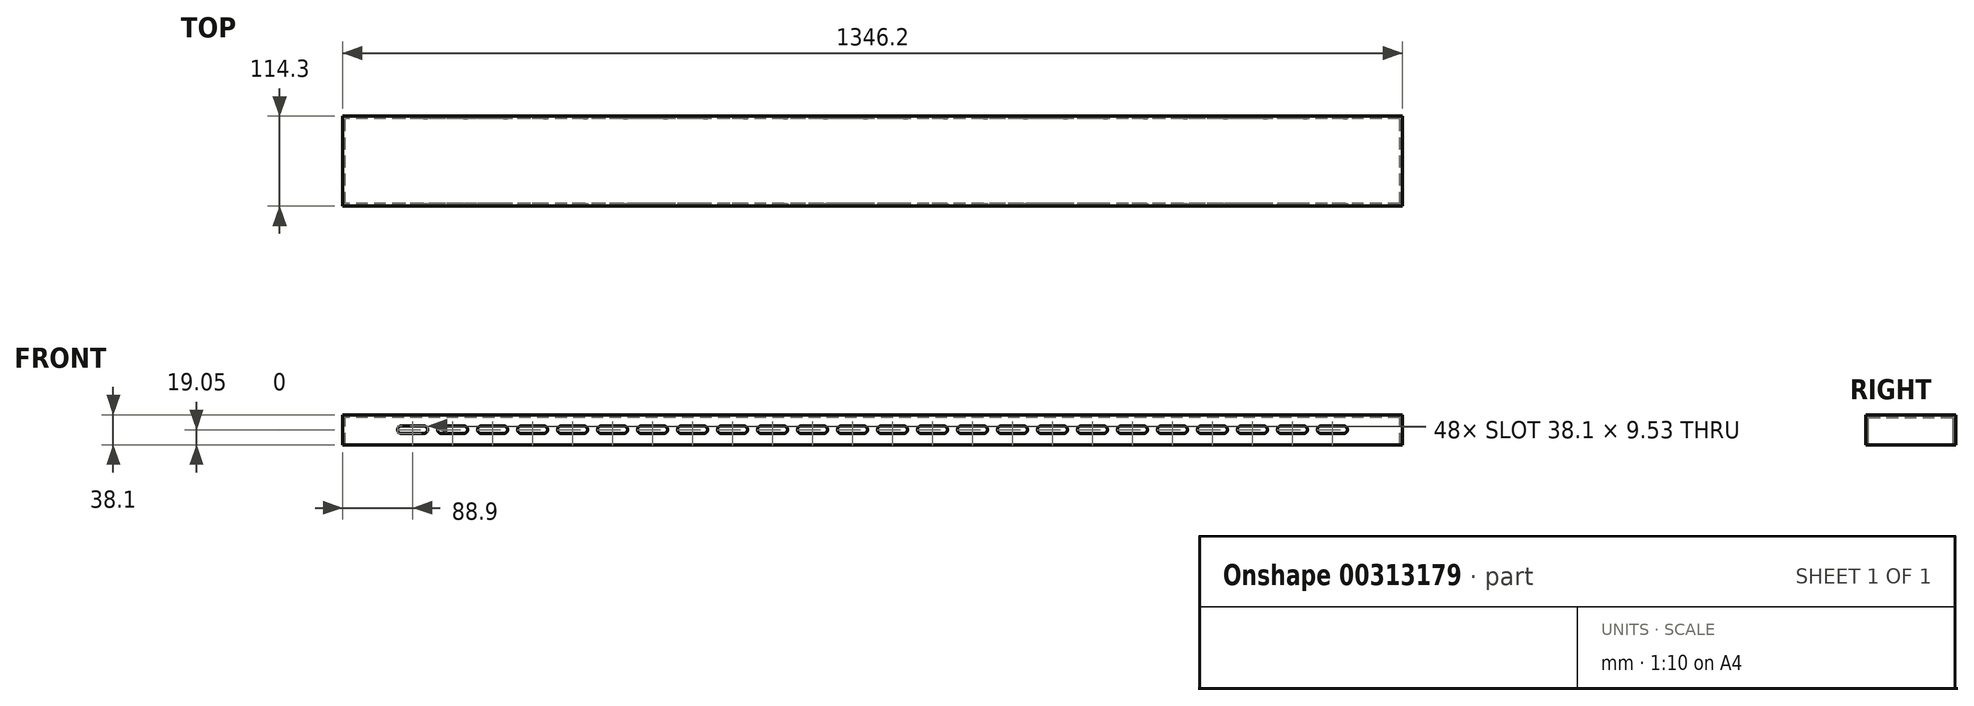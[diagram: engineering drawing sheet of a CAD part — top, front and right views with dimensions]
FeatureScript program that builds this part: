
annotation { "Feature Type Name" : "Feature", "Feature Type Description" : "" }
export const myFeature = defineFeature(function(context is Context, id is Id, definition is map)
    precondition{}
    {
        {
            var Q0;
            Q0=qCreatedBy(makeId("Right.planeOp"),FACE);
            var sketch = newSketch(context, id + "F0", { "sketchPlane" : qUnion([Q0])});
            skLineSegment(sketch, "E0.bottom", {"start": v(0, 0) * mm, "end": v(114.3, 0) * mm});
            skLineSegment(sketch, "E0.top", {"start": v(0, 38.1) * mm, "end": v(114.3, 38.1) * mm});
            skLineSegment(sketch, "E0.left", {"start": v(0, 0) * mm, "end": v(0, 38.1) * mm});
            skLineSegment(sketch, "E0.right", {"start": v(114.3, 0) * mm, "end": v(114.3, 38.1) * mm});
            skSolve(sketch);
        }
        {
            var Q0;
            Q0=qSketchRegion(id+"F0",true);
            extrude(context, id + "F1", {"entities" : qUnion([Q0]), "endBound" : BoundingType.SYMMETRIC, "depth" : 1346.2 * mm});
        }
        {
            var Q0;
            Q0=makeQuery(id+"F1.opExtrude","SWEPT_FACE",FACE,{"disambiguationData":[OSD([sQuery(id+"F0.wireOp",EDGE,"E0.bottom")])]});
            shell(context, id + "F2", {"entities" : qUnion([Q0]), "thickness" : 3.17 * mm});
        }
        {
            var Q0;
            Q0=makeQuery(id+"F1.opExtrude","SWEPT_FACE",FACE,{"disambiguationData":[OSD([sQuery(id+"F0.wireOp",EDGE,"E0.left")])]});
            var sketch = newSketch(context, id + "F3", { "sketchPlane" : qUnion([Q0])});
            skPoint(sketch, "E1.centerSnap0", {"position": v(-673.1, 19.05) * mm});
            skLineSegment(sketch, "E2.bottom", {"start": v(-569.91, 14.29) * mm, "end": v(-598.49, 14.29) * mm});
            skLineSegment(sketch, "E2.top", {"start": v(-569.91, 23.81) * mm, "end": v(-598.49, 23.81) * mm});
            skLineSegment(sketch, "E2.left", {"start": v(-565.15, 19.05) * mm, "end": v(-565.15, 19.05) * mm});
            skLineSegment(sketch, "E2.right", {"start": v(-603.25, 19.05) * mm, "end": v(-603.25, 19.05) * mm});
            skPoint(sketch, "E2.middle", {"position": v(-584.2, 19.05) * mm});
            skPoint(sketch, "E3.visualSharp", {"position": v(-565.15, 23.81) * mm});
            skArc(sketch, "E3.filletArc", {"start": v(-565.15, 19.05) * mm, "mid": v(-566.54, 22.42) * mm, "end": v(-569.91, 23.81) * mm});
            skPoint(sketch, "E4.visualSharp", {"position": v(-565.15, 14.29) * mm});
            skArc(sketch, "E4.filletArc", {"start": v(-569.91, 14.29) * mm, "mid": v(-566.54, 15.68) * mm, "end": v(-565.15, 19.05) * mm});
            skPoint(sketch, "E5.visualSharp", {"position": v(-603.25, 23.81) * mm});
            skArc(sketch, "E5.filletArc", {"start": v(-598.49, 23.81) * mm, "mid": v(-601.86, 22.42) * mm, "end": v(-603.25, 19.05) * mm});
            skPoint(sketch, "E6.visualSharp", {"position": v(-603.25, 14.29) * mm});
            skArc(sketch, "E6.filletArc", {"start": v(-603.25, 19.05) * mm, "mid": v(-601.86, 15.68) * mm, "end": v(-598.49, 14.29) * mm});
            skPoint(sketch, "E7.1.0.0", {"position": v(-514.35, 14.29) * mm});
            skPoint(sketch, "E7.1.0.1", {"position": v(-514.35, 23.81) * mm});
            skLineSegment(sketch, "E7.1.0.2", {"start": v(-519.11, 23.81) * mm, "end": v(-547.69, 23.81) * mm});
            skPoint(sketch, "E7.1.0.3", {"position": v(-552.45, 14.29) * mm});
            skLineSegment(sketch, "E7.1.0.4", {"start": v(-519.11, 14.29) * mm, "end": v(-547.69, 14.29) * mm});
            skPoint(sketch, "E7.1.0.5", {"position": v(-533.4, 19.05) * mm});
            skPoint(sketch, "E7.1.0.6", {"position": v(-552.45, 23.81) * mm});
            skArc(sketch, "E7.1.0.7", {"start": v(-514.35, 19.05) * mm, "mid": v(-515.74, 22.42) * mm, "end": v(-519.11, 23.81) * mm});
            skArc(sketch, "E7.1.0.8", {"start": v(-519.11, 14.29) * mm, "mid": v(-515.74, 15.68) * mm, "end": v(-514.35, 19.05) * mm});
            skArc(sketch, "E7.1.0.9", {"start": v(-552.45, 19.05) * mm, "mid": v(-551.06, 15.68) * mm, "end": v(-547.69, 14.29) * mm});
            skArc(sketch, "E7.1.0.10", {"start": v(-547.69, 23.81) * mm, "mid": v(-551.06, 22.42) * mm, "end": v(-552.45, 19.05) * mm});
            skPoint(sketch, "E7.2.0.0", {"position": v(-463.55, 14.29) * mm});
            skPoint(sketch, "E7.2.0.1", {"position": v(-463.55, 23.81) * mm});
            skLineSegment(sketch, "E7.2.0.2", {"start": v(-468.31, 23.81) * mm, "end": v(-496.89, 23.81) * mm});
            skPoint(sketch, "E7.2.0.3", {"position": v(-501.65, 14.29) * mm});
            skLineSegment(sketch, "E7.2.0.4", {"start": v(-468.31, 14.29) * mm, "end": v(-496.89, 14.29) * mm});
            skPoint(sketch, "E7.2.0.5", {"position": v(-482.6, 19.05) * mm});
            skPoint(sketch, "E7.2.0.6", {"position": v(-501.65, 23.81) * mm});
            skArc(sketch, "E7.2.0.7", {"start": v(-463.55, 19.05) * mm, "mid": v(-464.94, 22.42) * mm, "end": v(-468.31, 23.81) * mm});
            skArc(sketch, "E7.2.0.8", {"start": v(-468.31, 14.29) * mm, "mid": v(-464.94, 15.68) * mm, "end": v(-463.55, 19.05) * mm});
            skArc(sketch, "E7.2.0.9", {"start": v(-501.65, 19.05) * mm, "mid": v(-500.26, 15.68) * mm, "end": v(-496.89, 14.29) * mm});
            skArc(sketch, "E7.2.0.10", {"start": v(-496.89, 23.81) * mm, "mid": v(-500.26, 22.42) * mm, "end": v(-501.65, 19.05) * mm});
            skPoint(sketch, "E7.3.0.0", {"position": v(-412.75, 14.29) * mm});
            skPoint(sketch, "E7.3.0.1", {"position": v(-412.75, 23.81) * mm});
            skLineSegment(sketch, "E7.3.0.2", {"start": v(-417.51, 23.81) * mm, "end": v(-446.09, 23.81) * mm});
            skPoint(sketch, "E7.3.0.3", {"position": v(-450.85, 14.29) * mm});
            skLineSegment(sketch, "E7.3.0.4", {"start": v(-417.51, 14.29) * mm, "end": v(-446.09, 14.29) * mm});
            skPoint(sketch, "E7.3.0.5", {"position": v(-431.8, 19.05) * mm});
            skPoint(sketch, "E7.3.0.6", {"position": v(-450.85, 23.81) * mm});
            skArc(sketch, "E7.3.0.7", {"start": v(-412.75, 19.05) * mm, "mid": v(-414.14, 22.42) * mm, "end": v(-417.51, 23.81) * mm});
            skArc(sketch, "E7.3.0.8", {"start": v(-417.51, 14.29) * mm, "mid": v(-414.14, 15.68) * mm, "end": v(-412.75, 19.05) * mm});
            skArc(sketch, "E7.3.0.9", {"start": v(-450.85, 19.05) * mm, "mid": v(-449.46, 15.68) * mm, "end": v(-446.09, 14.29) * mm});
            skArc(sketch, "E7.3.0.10", {"start": v(-446.09, 23.81) * mm, "mid": v(-449.46, 22.42) * mm, "end": v(-450.85, 19.05) * mm});
            skPoint(sketch, "E7.4.0.0", {"position": v(-361.95, 14.29) * mm});
            skPoint(sketch, "E7.4.0.1", {"position": v(-361.95, 23.81) * mm});
            skLineSegment(sketch, "E7.4.0.2", {"start": v(-366.71, 23.81) * mm, "end": v(-395.29, 23.81) * mm});
            skPoint(sketch, "E7.4.0.3", {"position": v(-400.05, 14.29) * mm});
            skLineSegment(sketch, "E7.4.0.4", {"start": v(-366.71, 14.29) * mm, "end": v(-395.29, 14.29) * mm});
            skPoint(sketch, "E7.4.0.5", {"position": v(-381, 19.05) * mm});
            skPoint(sketch, "E7.4.0.6", {"position": v(-400.05, 23.81) * mm});
            skArc(sketch, "E7.4.0.7", {"start": v(-361.95, 19.05) * mm, "mid": v(-363.34, 22.42) * mm, "end": v(-366.71, 23.81) * mm});
            skArc(sketch, "E7.4.0.8", {"start": v(-366.71, 14.29) * mm, "mid": v(-363.34, 15.68) * mm, "end": v(-361.95, 19.05) * mm});
            skArc(sketch, "E7.4.0.9", {"start": v(-400.05, 19.05) * mm, "mid": v(-398.66, 15.68) * mm, "end": v(-395.29, 14.29) * mm});
            skArc(sketch, "E7.4.0.10", {"start": v(-395.29, 23.81) * mm, "mid": v(-398.66, 22.42) * mm, "end": v(-400.05, 19.05) * mm});
            skPoint(sketch, "E7.5.0.0", {"position": v(-311.15, 14.29) * mm});
            skPoint(sketch, "E7.5.0.1", {"position": v(-311.15, 23.81) * mm});
            skLineSegment(sketch, "E7.5.0.2", {"start": v(-315.91, 23.81) * mm, "end": v(-344.49, 23.81) * mm});
            skPoint(sketch, "E7.5.0.3", {"position": v(-349.25, 14.29) * mm});
            skLineSegment(sketch, "E7.5.0.4", {"start": v(-315.91, 14.29) * mm, "end": v(-344.49, 14.29) * mm});
            skPoint(sketch, "E7.5.0.5", {"position": v(-330.2, 19.05) * mm});
            skPoint(sketch, "E7.5.0.6", {"position": v(-349.25, 23.81) * mm});
            skArc(sketch, "E7.5.0.7", {"start": v(-311.15, 19.05) * mm, "mid": v(-312.54, 22.42) * mm, "end": v(-315.91, 23.81) * mm});
            skArc(sketch, "E7.5.0.8", {"start": v(-315.91, 14.29) * mm, "mid": v(-312.54, 15.68) * mm, "end": v(-311.15, 19.05) * mm});
            skArc(sketch, "E7.5.0.9", {"start": v(-349.25, 19.05) * mm, "mid": v(-347.86, 15.68) * mm, "end": v(-344.49, 14.29) * mm});
            skArc(sketch, "E7.5.0.10", {"start": v(-344.49, 23.81) * mm, "mid": v(-347.86, 22.42) * mm, "end": v(-349.25, 19.05) * mm});
            skPoint(sketch, "E7.6.0.0", {"position": v(-260.35, 14.29) * mm});
            skPoint(sketch, "E7.6.0.1", {"position": v(-260.35, 23.81) * mm});
            skLineSegment(sketch, "E7.6.0.2", {"start": v(-265.11, 23.81) * mm, "end": v(-293.69, 23.81) * mm});
            skPoint(sketch, "E7.6.0.3", {"position": v(-298.45, 14.29) * mm});
            skLineSegment(sketch, "E7.6.0.4", {"start": v(-265.11, 14.29) * mm, "end": v(-293.69, 14.29) * mm});
            skPoint(sketch, "E7.6.0.5", {"position": v(-279.4, 19.05) * mm});
            skPoint(sketch, "E7.6.0.6", {"position": v(-298.45, 23.81) * mm});
            skArc(sketch, "E7.6.0.7", {"start": v(-260.35, 19.05) * mm, "mid": v(-261.74, 22.42) * mm, "end": v(-265.11, 23.81) * mm});
            skArc(sketch, "E7.6.0.8", {"start": v(-265.11, 14.29) * mm, "mid": v(-261.74, 15.68) * mm, "end": v(-260.35, 19.05) * mm});
            skArc(sketch, "E7.6.0.9", {"start": v(-298.45, 19.05) * mm, "mid": v(-297.06, 15.68) * mm, "end": v(-293.69, 14.29) * mm});
            skArc(sketch, "E7.6.0.10", {"start": v(-293.69, 23.81) * mm, "mid": v(-297.06, 22.42) * mm, "end": v(-298.45, 19.05) * mm});
            skPoint(sketch, "E7.7.0.0", {"position": v(-209.55, 14.29) * mm});
            skPoint(sketch, "E7.7.0.1", {"position": v(-209.55, 23.81) * mm});
            skLineSegment(sketch, "E7.7.0.2", {"start": v(-214.31, 23.81) * mm, "end": v(-242.89, 23.81) * mm});
            skPoint(sketch, "E7.7.0.3", {"position": v(-247.65, 14.29) * mm});
            skLineSegment(sketch, "E7.7.0.4", {"start": v(-214.31, 14.29) * mm, "end": v(-242.89, 14.29) * mm});
            skPoint(sketch, "E7.7.0.5", {"position": v(-228.6, 19.05) * mm});
            skPoint(sketch, "E7.7.0.6", {"position": v(-247.65, 23.81) * mm});
            skArc(sketch, "E7.7.0.7", {"start": v(-209.55, 19.05) * mm, "mid": v(-210.94, 22.42) * mm, "end": v(-214.31, 23.81) * mm});
            skArc(sketch, "E7.7.0.8", {"start": v(-214.31, 14.29) * mm, "mid": v(-210.94, 15.68) * mm, "end": v(-209.55, 19.05) * mm});
            skArc(sketch, "E7.7.0.9", {"start": v(-247.65, 19.05) * mm, "mid": v(-246.26, 15.68) * mm, "end": v(-242.89, 14.29) * mm});
            skArc(sketch, "E7.7.0.10", {"start": v(-242.89, 23.81) * mm, "mid": v(-246.26, 22.42) * mm, "end": v(-247.65, 19.05) * mm});
            skPoint(sketch, "E7.8.0.0", {"position": v(-158.75, 14.29) * mm});
            skPoint(sketch, "E7.8.0.1", {"position": v(-158.75, 23.81) * mm});
            skLineSegment(sketch, "E7.8.0.2", {"start": v(-163.51, 23.81) * mm, "end": v(-192.09, 23.81) * mm});
            skPoint(sketch, "E7.8.0.3", {"position": v(-196.85, 14.29) * mm});
            skLineSegment(sketch, "E7.8.0.4", {"start": v(-163.51, 14.29) * mm, "end": v(-192.09, 14.29) * mm});
            skPoint(sketch, "E7.8.0.5", {"position": v(-177.8, 19.05) * mm});
            skPoint(sketch, "E7.8.0.6", {"position": v(-196.85, 23.81) * mm});
            skArc(sketch, "E7.8.0.7", {"start": v(-158.75, 19.05) * mm, "mid": v(-160.14, 22.42) * mm, "end": v(-163.51, 23.81) * mm});
            skArc(sketch, "E7.8.0.8", {"start": v(-163.51, 14.29) * mm, "mid": v(-160.14, 15.68) * mm, "end": v(-158.75, 19.05) * mm});
            skArc(sketch, "E7.8.0.9", {"start": v(-196.85, 19.05) * mm, "mid": v(-195.46, 15.68) * mm, "end": v(-192.09, 14.29) * mm});
            skArc(sketch, "E7.8.0.10", {"start": v(-192.09, 23.81) * mm, "mid": v(-195.46, 22.42) * mm, "end": v(-196.85, 19.05) * mm});
            skPoint(sketch, "E7.9.0.0", {"position": v(-107.95, 14.29) * mm});
            skPoint(sketch, "E7.9.0.1", {"position": v(-107.95, 23.81) * mm});
            skLineSegment(sketch, "E7.9.0.2", {"start": v(-112.71, 23.81) * mm, "end": v(-141.29, 23.81) * mm});
            skPoint(sketch, "E7.9.0.3", {"position": v(-146.05, 14.29) * mm});
            skLineSegment(sketch, "E7.9.0.4", {"start": v(-112.71, 14.29) * mm, "end": v(-141.29, 14.29) * mm});
            skPoint(sketch, "E7.9.0.5", {"position": v(-127, 19.05) * mm});
            skPoint(sketch, "E7.9.0.6", {"position": v(-146.05, 23.81) * mm});
            skArc(sketch, "E7.9.0.7", {"start": v(-107.95, 19.05) * mm, "mid": v(-109.34, 22.42) * mm, "end": v(-112.71, 23.81) * mm});
            skArc(sketch, "E7.9.0.8", {"start": v(-112.71, 14.29) * mm, "mid": v(-109.34, 15.68) * mm, "end": v(-107.95, 19.05) * mm});
            skArc(sketch, "E7.9.0.9", {"start": v(-146.05, 19.05) * mm, "mid": v(-144.66, 15.68) * mm, "end": v(-141.29, 14.29) * mm});
            skArc(sketch, "E7.9.0.10", {"start": v(-141.29, 23.81) * mm, "mid": v(-144.66, 22.42) * mm, "end": v(-146.05, 19.05) * mm});
            skPoint(sketch, "E7.10.0.0", {"position": v(-57.15, 14.29) * mm});
            skPoint(sketch, "E7.10.0.1", {"position": v(-57.15, 23.81) * mm});
            skLineSegment(sketch, "E7.10.0.2", {"start": v(-61.91, 23.81) * mm, "end": v(-90.49, 23.81) * mm});
            skPoint(sketch, "E7.10.0.3", {"position": v(-95.25, 14.29) * mm});
            skLineSegment(sketch, "E7.10.0.4", {"start": v(-61.91, 14.29) * mm, "end": v(-90.49, 14.29) * mm});
            skPoint(sketch, "E7.10.0.5", {"position": v(-76.2, 19.05) * mm});
            skPoint(sketch, "E7.10.0.6", {"position": v(-95.25, 23.81) * mm});
            skArc(sketch, "E7.10.0.7", {"start": v(-57.15, 19.05) * mm, "mid": v(-58.54, 22.42) * mm, "end": v(-61.91, 23.81) * mm});
            skArc(sketch, "E7.10.0.8", {"start": v(-61.91, 14.29) * mm, "mid": v(-58.54, 15.68) * mm, "end": v(-57.15, 19.05) * mm});
            skArc(sketch, "E7.10.0.9", {"start": v(-95.25, 19.05) * mm, "mid": v(-93.86, 15.68) * mm, "end": v(-90.49, 14.29) * mm});
            skArc(sketch, "E7.10.0.10", {"start": v(-90.49, 23.81) * mm, "mid": v(-93.86, 22.42) * mm, "end": v(-95.25, 19.05) * mm});
            skPoint(sketch, "E7.11.0.0", {"position": v(-6.35, 14.29) * mm});
            skPoint(sketch, "E7.11.0.1", {"position": v(-6.35, 23.81) * mm});
            skLineSegment(sketch, "E7.11.0.2", {"start": v(-11.11, 23.81) * mm, "end": v(-39.69, 23.81) * mm});
            skPoint(sketch, "E7.11.0.3", {"position": v(-44.45, 14.29) * mm});
            skLineSegment(sketch, "E7.11.0.4", {"start": v(-11.11, 14.29) * mm, "end": v(-39.69, 14.29) * mm});
            skPoint(sketch, "E7.11.0.5", {"position": v(-25.4, 19.05) * mm});
            skPoint(sketch, "E7.11.0.6", {"position": v(-44.45, 23.81) * mm});
            skArc(sketch, "E7.11.0.7", {"start": v(-6.35, 19.05) * mm, "mid": v(-7.74, 22.42) * mm, "end": v(-11.11, 23.81) * mm});
            skArc(sketch, "E7.11.0.8", {"start": v(-11.11, 14.29) * mm, "mid": v(-7.74, 15.68) * mm, "end": v(-6.35, 19.05) * mm});
            skArc(sketch, "E7.11.0.9", {"start": v(-44.45, 19.05) * mm, "mid": v(-43.06, 15.68) * mm, "end": v(-39.69, 14.29) * mm});
            skArc(sketch, "E7.11.0.10", {"start": v(-39.69, 23.81) * mm, "mid": v(-43.06, 22.42) * mm, "end": v(-44.45, 19.05) * mm});
            skPoint(sketch, "E7.12.0.0", {"position": v(44.45, 14.29) * mm});
            skPoint(sketch, "E7.12.0.1", {"position": v(44.45, 23.81) * mm});
            skLineSegment(sketch, "E7.12.0.2", {"start": v(39.69, 23.81) * mm, "end": v(11.11, 23.81) * mm});
            skPoint(sketch, "E7.12.0.3", {"position": v(6.35, 14.29) * mm});
            skLineSegment(sketch, "E7.12.0.4", {"start": v(39.69, 14.29) * mm, "end": v(11.11, 14.29) * mm});
            skPoint(sketch, "E7.12.0.5", {"position": v(25.4, 19.05) * mm});
            skPoint(sketch, "E7.12.0.6", {"position": v(6.35, 23.81) * mm});
            skArc(sketch, "E7.12.0.7", {"start": v(44.45, 19.05) * mm, "mid": v(43.06, 22.42) * mm, "end": v(39.69, 23.81) * mm});
            skArc(sketch, "E7.12.0.8", {"start": v(39.69, 14.29) * mm, "mid": v(43.06, 15.68) * mm, "end": v(44.45, 19.05) * mm});
            skArc(sketch, "E7.12.0.9", {"start": v(6.35, 19.05) * mm, "mid": v(7.74, 15.68) * mm, "end": v(11.11, 14.29) * mm});
            skArc(sketch, "E7.12.0.10", {"start": v(11.11, 23.81) * mm, "mid": v(7.74, 22.42) * mm, "end": v(6.35, 19.05) * mm});
            skPoint(sketch, "E7.13.0.0", {"position": v(95.25, 14.29) * mm});
            skPoint(sketch, "E7.13.0.1", {"position": v(95.25, 23.81) * mm});
            skLineSegment(sketch, "E7.13.0.2", {"start": v(90.49, 23.81) * mm, "end": v(61.91, 23.81) * mm});
            skPoint(sketch, "E7.13.0.3", {"position": v(57.15, 14.29) * mm});
            skLineSegment(sketch, "E7.13.0.4", {"start": v(90.49, 14.29) * mm, "end": v(61.91, 14.29) * mm});
            skPoint(sketch, "E7.13.0.5", {"position": v(76.2, 19.05) * mm});
            skPoint(sketch, "E7.13.0.6", {"position": v(57.15, 23.81) * mm});
            skArc(sketch, "E7.13.0.7", {"start": v(95.25, 19.05) * mm, "mid": v(93.86, 22.42) * mm, "end": v(90.49, 23.81) * mm});
            skArc(sketch, "E7.13.0.8", {"start": v(90.49, 14.29) * mm, "mid": v(93.86, 15.68) * mm, "end": v(95.25, 19.05) * mm});
            skArc(sketch, "E7.13.0.9", {"start": v(57.15, 19.05) * mm, "mid": v(58.54, 15.68) * mm, "end": v(61.91, 14.29) * mm});
            skArc(sketch, "E7.13.0.10", {"start": v(61.91, 23.81) * mm, "mid": v(58.54, 22.42) * mm, "end": v(57.15, 19.05) * mm});
            skPoint(sketch, "E7.14.0.0", {"position": v(146.05, 14.29) * mm});
            skPoint(sketch, "E7.14.0.1", {"position": v(146.05, 23.81) * mm});
            skLineSegment(sketch, "E7.14.0.2", {"start": v(141.29, 23.81) * mm, "end": v(112.71, 23.81) * mm});
            skPoint(sketch, "E7.14.0.3", {"position": v(107.95, 14.29) * mm});
            skLineSegment(sketch, "E7.14.0.4", {"start": v(141.29, 14.29) * mm, "end": v(112.71, 14.29) * mm});
            skPoint(sketch, "E7.14.0.5", {"position": v(127, 19.05) * mm});
            skPoint(sketch, "E7.14.0.6", {"position": v(107.95, 23.81) * mm});
            skArc(sketch, "E7.14.0.7", {"start": v(146.05, 19.05) * mm, "mid": v(144.66, 22.42) * mm, "end": v(141.29, 23.81) * mm});
            skArc(sketch, "E7.14.0.8", {"start": v(141.29, 14.29) * mm, "mid": v(144.66, 15.68) * mm, "end": v(146.05, 19.05) * mm});
            skArc(sketch, "E7.14.0.9", {"start": v(107.95, 19.05) * mm, "mid": v(109.34, 15.68) * mm, "end": v(112.71, 14.29) * mm});
            skArc(sketch, "E7.14.0.10", {"start": v(112.71, 23.81) * mm, "mid": v(109.34, 22.42) * mm, "end": v(107.95, 19.05) * mm});
            skPoint(sketch, "E7.15.0.0", {"position": v(196.85, 14.29) * mm});
            skPoint(sketch, "E7.15.0.1", {"position": v(196.85, 23.81) * mm});
            skLineSegment(sketch, "E7.15.0.2", {"start": v(192.09, 23.81) * mm, "end": v(163.51, 23.81) * mm});
            skPoint(sketch, "E7.15.0.3", {"position": v(158.75, 14.29) * mm});
            skLineSegment(sketch, "E7.15.0.4", {"start": v(192.09, 14.29) * mm, "end": v(163.51, 14.29) * mm});
            skPoint(sketch, "E7.15.0.5", {"position": v(177.8, 19.05) * mm});
            skPoint(sketch, "E7.15.0.6", {"position": v(158.75, 23.81) * mm});
            skArc(sketch, "E7.15.0.7", {"start": v(196.85, 19.05) * mm, "mid": v(195.46, 22.42) * mm, "end": v(192.09, 23.81) * mm});
            skArc(sketch, "E7.15.0.8", {"start": v(192.09, 14.29) * mm, "mid": v(195.46, 15.68) * mm, "end": v(196.85, 19.05) * mm});
            skArc(sketch, "E7.15.0.9", {"start": v(158.75, 19.05) * mm, "mid": v(160.14, 15.68) * mm, "end": v(163.51, 14.29) * mm});
            skArc(sketch, "E7.15.0.10", {"start": v(163.51, 23.81) * mm, "mid": v(160.14, 22.42) * mm, "end": v(158.75, 19.05) * mm});
            skPoint(sketch, "E7.16.0.0", {"position": v(247.65, 14.29) * mm});
            skPoint(sketch, "E7.16.0.1", {"position": v(247.65, 23.81) * mm});
            skLineSegment(sketch, "E7.16.0.2", {"start": v(242.89, 23.81) * mm, "end": v(214.31, 23.81) * mm});
            skPoint(sketch, "E7.16.0.3", {"position": v(209.55, 14.29) * mm});
            skLineSegment(sketch, "E7.16.0.4", {"start": v(242.89, 14.29) * mm, "end": v(214.31, 14.29) * mm});
            skPoint(sketch, "E7.16.0.5", {"position": v(228.6, 19.05) * mm});
            skPoint(sketch, "E7.16.0.6", {"position": v(209.55, 23.81) * mm});
            skArc(sketch, "E7.16.0.7", {"start": v(247.65, 19.05) * mm, "mid": v(246.26, 22.42) * mm, "end": v(242.89, 23.81) * mm});
            skArc(sketch, "E7.16.0.8", {"start": v(242.89, 14.29) * mm, "mid": v(246.26, 15.68) * mm, "end": v(247.65, 19.05) * mm});
            skArc(sketch, "E7.16.0.9", {"start": v(209.55, 19.05) * mm, "mid": v(210.94, 15.68) * mm, "end": v(214.31, 14.29) * mm});
            skArc(sketch, "E7.16.0.10", {"start": v(214.31, 23.81) * mm, "mid": v(210.94, 22.42) * mm, "end": v(209.55, 19.05) * mm});
            skPoint(sketch, "E7.17.0.0", {"position": v(298.45, 14.29) * mm});
            skPoint(sketch, "E7.17.0.1", {"position": v(298.45, 23.81) * mm});
            skLineSegment(sketch, "E7.17.0.2", {"start": v(293.69, 23.81) * mm, "end": v(265.11, 23.81) * mm});
            skPoint(sketch, "E7.17.0.3", {"position": v(260.35, 14.29) * mm});
            skLineSegment(sketch, "E7.17.0.4", {"start": v(293.69, 14.29) * mm, "end": v(265.11, 14.29) * mm});
            skPoint(sketch, "E7.17.0.5", {"position": v(279.4, 19.05) * mm});
            skPoint(sketch, "E7.17.0.6", {"position": v(260.35, 23.81) * mm});
            skArc(sketch, "E7.17.0.7", {"start": v(298.45, 19.05) * mm, "mid": v(297.06, 22.42) * mm, "end": v(293.69, 23.81) * mm});
            skArc(sketch, "E7.17.0.8", {"start": v(293.69, 14.29) * mm, "mid": v(297.06, 15.68) * mm, "end": v(298.45, 19.05) * mm});
            skArc(sketch, "E7.17.0.9", {"start": v(260.35, 19.05) * mm, "mid": v(261.74, 15.68) * mm, "end": v(265.11, 14.29) * mm});
            skArc(sketch, "E7.17.0.10", {"start": v(265.11, 23.81) * mm, "mid": v(261.74, 22.42) * mm, "end": v(260.35, 19.05) * mm});
            skPoint(sketch, "E7.18.0.0", {"position": v(349.25, 14.29) * mm});
            skPoint(sketch, "E7.18.0.1", {"position": v(349.25, 23.81) * mm});
            skLineSegment(sketch, "E7.18.0.2", {"start": v(344.49, 23.81) * mm, "end": v(315.91, 23.81) * mm});
            skPoint(sketch, "E7.18.0.3", {"position": v(311.15, 14.29) * mm});
            skLineSegment(sketch, "E7.18.0.4", {"start": v(344.49, 14.29) * mm, "end": v(315.91, 14.29) * mm});
            skPoint(sketch, "E7.18.0.5", {"position": v(330.2, 19.05) * mm});
            skPoint(sketch, "E7.18.0.6", {"position": v(311.15, 23.81) * mm});
            skArc(sketch, "E7.18.0.7", {"start": v(349.25, 19.05) * mm, "mid": v(347.86, 22.42) * mm, "end": v(344.49, 23.81) * mm});
            skArc(sketch, "E7.18.0.8", {"start": v(344.49, 14.29) * mm, "mid": v(347.86, 15.68) * mm, "end": v(349.25, 19.05) * mm});
            skArc(sketch, "E7.18.0.9", {"start": v(311.15, 19.05) * mm, "mid": v(312.54, 15.68) * mm, "end": v(315.91, 14.29) * mm});
            skArc(sketch, "E7.18.0.10", {"start": v(315.91, 23.81) * mm, "mid": v(312.54, 22.42) * mm, "end": v(311.15, 19.05) * mm});
            skPoint(sketch, "E7.19.0.0", {"position": v(400.05, 14.29) * mm});
            skPoint(sketch, "E7.19.0.1", {"position": v(400.05, 23.81) * mm});
            skLineSegment(sketch, "E7.19.0.2", {"start": v(395.29, 23.81) * mm, "end": v(366.71, 23.81) * mm});
            skPoint(sketch, "E7.19.0.3", {"position": v(361.95, 14.29) * mm});
            skLineSegment(sketch, "E7.19.0.4", {"start": v(395.29, 14.29) * mm, "end": v(366.71, 14.29) * mm});
            skPoint(sketch, "E7.19.0.5", {"position": v(381, 19.05) * mm});
            skPoint(sketch, "E7.19.0.6", {"position": v(361.95, 23.81) * mm});
            skArc(sketch, "E7.19.0.7", {"start": v(400.05, 19.05) * mm, "mid": v(398.66, 22.42) * mm, "end": v(395.29, 23.81) * mm});
            skArc(sketch, "E7.19.0.8", {"start": v(395.29, 14.29) * mm, "mid": v(398.66, 15.68) * mm, "end": v(400.05, 19.05) * mm});
            skArc(sketch, "E7.19.0.9", {"start": v(361.95, 19.05) * mm, "mid": v(363.34, 15.68) * mm, "end": v(366.71, 14.29) * mm});
            skArc(sketch, "E7.19.0.10", {"start": v(366.71, 23.81) * mm, "mid": v(363.34, 22.42) * mm, "end": v(361.95, 19.05) * mm});
            skPoint(sketch, "E7.20.0.0", {"position": v(450.85, 14.29) * mm});
            skPoint(sketch, "E7.20.0.1", {"position": v(450.85, 23.81) * mm});
            skLineSegment(sketch, "E7.20.0.2", {"start": v(446.09, 23.81) * mm, "end": v(417.51, 23.81) * mm});
            skPoint(sketch, "E7.20.0.3", {"position": v(412.75, 14.29) * mm});
            skLineSegment(sketch, "E7.20.0.4", {"start": v(446.09, 14.29) * mm, "end": v(417.51, 14.29) * mm});
            skPoint(sketch, "E7.20.0.5", {"position": v(431.8, 19.05) * mm});
            skPoint(sketch, "E7.20.0.6", {"position": v(412.75, 23.81) * mm});
            skArc(sketch, "E7.20.0.7", {"start": v(450.85, 19.05) * mm, "mid": v(449.46, 22.42) * mm, "end": v(446.09, 23.81) * mm});
            skArc(sketch, "E7.20.0.8", {"start": v(446.09, 14.29) * mm, "mid": v(449.46, 15.68) * mm, "end": v(450.85, 19.05) * mm});
            skArc(sketch, "E7.20.0.9", {"start": v(412.75, 19.05) * mm, "mid": v(414.14, 15.68) * mm, "end": v(417.51, 14.29) * mm});
            skArc(sketch, "E7.20.0.10", {"start": v(417.51, 23.81) * mm, "mid": v(414.14, 22.42) * mm, "end": v(412.75, 19.05) * mm});
            skPoint(sketch, "E7.21.0.0", {"position": v(501.65, 14.29) * mm});
            skPoint(sketch, "E7.21.0.1", {"position": v(501.65, 23.81) * mm});
            skLineSegment(sketch, "E7.21.0.2", {"start": v(496.89, 23.81) * mm, "end": v(468.31, 23.81) * mm});
            skPoint(sketch, "E7.21.0.3", {"position": v(463.55, 14.29) * mm});
            skLineSegment(sketch, "E7.21.0.4", {"start": v(496.89, 14.29) * mm, "end": v(468.31, 14.29) * mm});
            skPoint(sketch, "E7.21.0.5", {"position": v(482.6, 19.05) * mm});
            skPoint(sketch, "E7.21.0.6", {"position": v(463.55, 23.81) * mm});
            skArc(sketch, "E7.21.0.7", {"start": v(501.65, 19.05) * mm, "mid": v(500.26, 22.42) * mm, "end": v(496.89, 23.81) * mm});
            skArc(sketch, "E7.21.0.8", {"start": v(496.89, 14.29) * mm, "mid": v(500.26, 15.68) * mm, "end": v(501.65, 19.05) * mm});
            skArc(sketch, "E7.21.0.9", {"start": v(463.55, 19.05) * mm, "mid": v(464.94, 15.68) * mm, "end": v(468.31, 14.29) * mm});
            skArc(sketch, "E7.21.0.10", {"start": v(468.31, 23.81) * mm, "mid": v(464.94, 22.42) * mm, "end": v(463.55, 19.05) * mm});
            skPoint(sketch, "E7.22.0.0", {"position": v(552.45, 14.29) * mm});
            skPoint(sketch, "E7.22.0.1", {"position": v(552.45, 23.81) * mm});
            skLineSegment(sketch, "E7.22.0.2", {"start": v(547.69, 23.81) * mm, "end": v(519.11, 23.81) * mm});
            skPoint(sketch, "E7.22.0.3", {"position": v(514.35, 14.29) * mm});
            skLineSegment(sketch, "E7.22.0.4", {"start": v(547.69, 14.29) * mm, "end": v(519.11, 14.29) * mm});
            skPoint(sketch, "E7.22.0.5", {"position": v(533.4, 19.05) * mm});
            skPoint(sketch, "E7.22.0.6", {"position": v(514.35, 23.81) * mm});
            skArc(sketch, "E7.22.0.7", {"start": v(552.45, 19.05) * mm, "mid": v(551.06, 22.42) * mm, "end": v(547.69, 23.81) * mm});
            skArc(sketch, "E7.22.0.8", {"start": v(547.69, 14.29) * mm, "mid": v(551.06, 15.68) * mm, "end": v(552.45, 19.05) * mm});
            skArc(sketch, "E7.22.0.9", {"start": v(514.35, 19.05) * mm, "mid": v(515.74, 15.68) * mm, "end": v(519.11, 14.29) * mm});
            skArc(sketch, "E7.22.0.10", {"start": v(519.11, 23.81) * mm, "mid": v(515.74, 22.42) * mm, "end": v(514.35, 19.05) * mm});
            skPoint(sketch, "E7.23.0.0", {"position": v(603.25, 14.29) * mm});
            skPoint(sketch, "E7.23.0.1", {"position": v(603.25, 23.81) * mm});
            skLineSegment(sketch, "E7.23.0.2", {"start": v(598.49, 23.81) * mm, "end": v(569.91, 23.81) * mm});
            skPoint(sketch, "E7.23.0.3", {"position": v(565.15, 14.29) * mm});
            skLineSegment(sketch, "E7.23.0.4", {"start": v(598.49, 14.29) * mm, "end": v(569.91, 14.29) * mm});
            skPoint(sketch, "E7.23.0.5", {"position": v(584.2, 19.05) * mm});
            skPoint(sketch, "E7.23.0.6", {"position": v(565.15, 23.81) * mm});
            skArc(sketch, "E7.23.0.7", {"start": v(603.25, 19.05) * mm, "mid": v(601.86, 22.42) * mm, "end": v(598.49, 23.81) * mm});
            skArc(sketch, "E7.23.0.8", {"start": v(598.49, 14.29) * mm, "mid": v(601.86, 15.68) * mm, "end": v(603.25, 19.05) * mm});
            skArc(sketch, "E7.23.0.9", {"start": v(565.15, 19.05) * mm, "mid": v(566.54, 15.68) * mm, "end": v(569.91, 14.29) * mm});
            skArc(sketch, "E7.23.0.10", {"start": v(569.91, 23.81) * mm, "mid": v(566.54, 22.42) * mm, "end": v(565.15, 19.05) * mm});
            skLineSegment(sketch, "E7.direction1", {"start": v(-584.2, 19.05) * mm, "end": v(-533.4, 19.05) * mm, "construction": true});
            skSolve(sketch);
        }
        {
            var Q0;
            Q0 = qSketchRegion(id + "F3", true);
            extrude(context, id + "F4", {"entities" : qUnion([Q0]), "operationType" : NewBodyOperationType.REMOVE, "endBound" : BoundingType.THROUGH_ALL, "oppositeDirection" : true, "depth" : 25.4 * mm});
        }
    });
